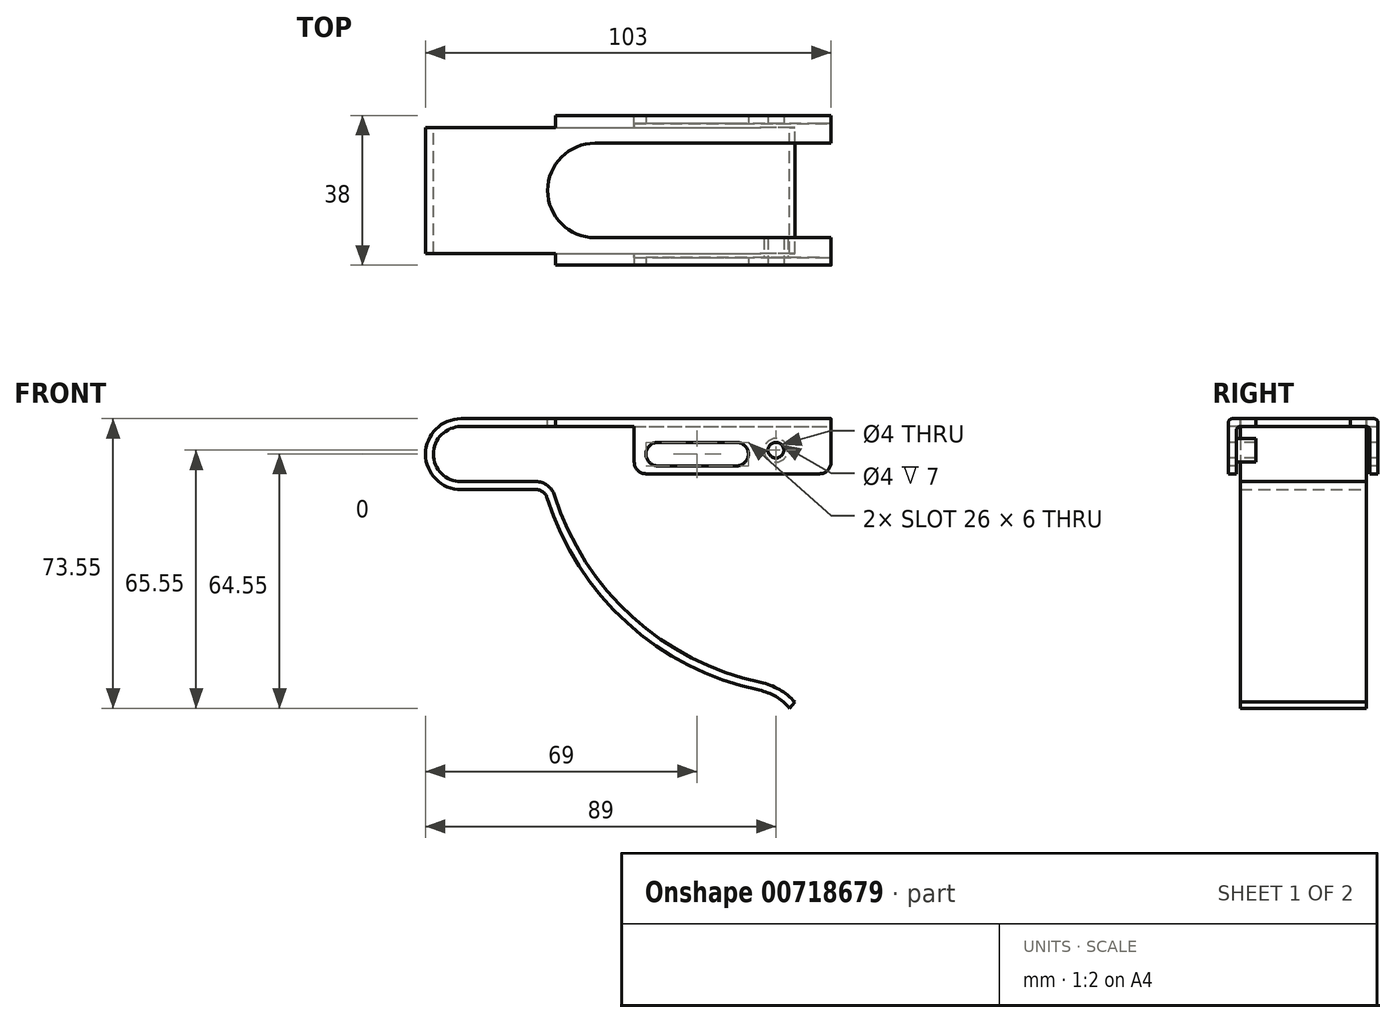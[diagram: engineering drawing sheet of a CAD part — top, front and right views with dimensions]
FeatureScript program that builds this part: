
annotation { "Feature Type Name" : "Feature", "Feature Type Description" : "" }
export const myFeature = defineFeature(function(context is Context, id is Id, definition is map)
    precondition{}
    {
        {
            var Q0;
            Q0=qCreatedBy(makeId("Front.planeOp"),FACE);
            var sketch = newSketch(context, id + "F0", { "sketchPlane" : qUnion([Q0])});
            skArc(sketch, "E0", {"start": v(0, 9) * mm, "mid": v(-9, 0) * mm, "end": v(0, -9) * mm});
            skLineSegment(sketch, "E1", {"start": v(0, -9) * mm, "end": v(19, -9) * mm});
            skLineSegment(sketch, "E2", {"start": v(0, 9) * mm, "end": v(94, 9) * mm});
            skArc(sketch, "E3", {"start": v(21.86, -11.1) * mm, "mid": v(42.18, -42.83) * mm, "end": v(75.74, -59.96) * mm});
            skArc(sketch, "E4", {"start": v(83.5, -64.55) * mm, "mid": v(80, -61.61) * mm, "end": v(75.74, -59.96) * mm});
            skPoint(sketch, "E5.visualSharp", {"position": v(21.24, -9) * mm});
            skArc(sketch, "E5.filletArc", {"start": v(21.86, -11.1) * mm, "mid": v(20.77, -9.58) * mm, "end": v(19, -9) * mm});
            skLineSegment(sketch, "E6.0", {"start": v(0, 7) * mm, "end": v(94, 7) * mm});
            skArc(sketch, "E6.1", {"start": v(0, 7) * mm, "mid": v(-7, 0) * mm, "end": v(0, -7) * mm});
            skArc(sketch, "E6.2", {"start": v(84.8, -63) * mm, "mid": v(80.87, -59.8) * mm, "end": v(76.15, -58) * mm});
            skArc(sketch, "E6.3", {"start": v(23.77, -10.5) * mm, "mid": v(43.52, -41.35) * mm, "end": v(76.15, -58) * mm});
            skArc(sketch, "E6.4", {"start": v(23.77, -10.5) * mm, "mid": v(21.96, -7.97) * mm, "end": v(19, -7) * mm});
            skLineSegment(sketch, "E6.5", {"start": v(0, -7) * mm, "end": v(19, -7) * mm});
            skLineSegment(sketch, "E7", {"start": v(83.5, -64.55) * mm, "end": v(84.8, -63) * mm});
            skLineSegment(sketch, "E8", {"start": v(94, 9) * mm, "end": v(94, 7) * mm});
            skSolve(sketch);
        }
        {
            var Q0;
            Q0 = qSketchRegion(id + "F0", true);
            extrude(context, id + "F1", {"entities" : qUnion([Q0]), "depth" : 16 * mm, "offsetDistance" : 25 * mm});
        }
        {
            var Q0;
            Q0=makeQuery(id+"F1.opExtrude","SWEPT_FACE",FACE,{"disambiguationData":[OSD([sQuery(id+"F0.wireOp",EDGE,"E2")])]});
            var sketch = newSketch(context, id + "F2", { "sketchPlane" : qUnion([Q0])});
            skLineSegment(sketch, "E9.bottom", {"start": v(94, -16) * mm, "end": v(24, -16) * mm});
            skLineSegment(sketch, "E9.top", {"start": v(94, -19) * mm, "end": v(24, -19) * mm});
            skLineSegment(sketch, "E9.left", {"start": v(94, -16) * mm, "end": v(94, -19) * mm});
            skLineSegment(sketch, "E9.right", {"start": v(24, -16) * mm, "end": v(24, -19) * mm});
            skSolve(sketch);
        }
        {
            var Q0;
            Q0 = qSketchRegion(id + "F2", true);
            extrude(context, id + "F3", {"entities" : qUnion([Q0]), "operationType" : NewBodyOperationType.ADD, "oppositeDirection" : true, "depth" : 2 * mm, "offsetDistance" : 25 * mm});
        }
        {
            var Q0;
            Q0=makeQuery(id+"F3.opExtrude","SWEPT_FACE",FACE,{"disambiguationData":[OSD([sQuery(id+"F2.wireOp",EDGE,"E9.top")])]});
            var sketch = newSketch(context, id + "F4", { "sketchPlane" : qUnion([Q0])});
            skLineSegment(sketch, "E10.bottom", {"start": v(94, 9) * mm, "end": v(44, 9) * mm});
            skLineSegment(sketch, "E10.top", {"start": v(94, -5) * mm, "end": v(44, -5) * mm});
            skLineSegment(sketch, "E10.left", {"start": v(94, 9) * mm, "end": v(94, -5) * mm});
            skLineSegment(sketch, "E10.right", {"start": v(44, 9) * mm, "end": v(44, -5) * mm});
            skSolve(sketch);
        }
        {
            var Q0;
            Q0 = qSketchRegion(id + "F4", true);
            extrude(context, id + "F5", {"entities" : qUnion([Q0]), "operationType" : NewBodyOperationType.ADD, "oppositeDirection" : true, "depth" : 2 * mm, "offsetDistance" : 25 * mm});
        }
        {
            var Q0;
            Q0=makeQuery(id+"F3.opExtrude","CAP_EDGE",EDGE,{"disambiguationData":[OSD([sQuery(id+"F2.wireOp",EDGE,"E9.top")])],"isStart":true});
            var Q1;
            Q1=makeQuery(id+"F5.boolean.opBoolean","INTERSECT",EDGE,{"derivedFrom":[makeQuery(id+"F3.boolean.opBoolean","MERGE",FACE,{"derivedFrom":[makeQuery(id+"F1.opExtrude","SWEPT_FACE",FACE,{"disambiguationData":[OSD([sQuery(id+"F0.wireOp",EDGE,"E6.0")])]}),makeQuery(id+"F3.opExtrude","CAP_FACE",FACE,{"disambiguationData":[OSD([sQuery(id+"F2.wireOp",EDGE,"E9.bottom"),sQuery(id+"F2.wireOp",EDGE,"E9.top"),sQuery(id+"F2.wireOp",EDGE,"E9.left"),sQuery(id+"F2.wireOp",EDGE,"E9.right")])],"isStart":false})]}),makeQuery(id+"F5.opExtrude","CAP_FACE",FACE,{"disambiguationData":[OSD([sQuery(id+"F4.wireOp",EDGE,"E10.bottom"),sQuery(id+"F4.wireOp",EDGE,"E10.top"),sQuery(id+"F4.wireOp",EDGE,"E10.left"),sQuery(id+"F4.wireOp",EDGE,"E10.right")])],"isStart":false})]});
            fillet(context, id + "F6", {"entities" : qUnion([Q0, Q1]), "radius" : 1 * mm, "allowEdgeOverflow" : false});
        }
        {
            var Q0;
            Q0=makeQuery(id+"F1.opExtrude","SWEPT_BODY",BODY,{"disambiguationData":[OSD([sQuery(id+"F0.wireOp",EDGE,"E0"),sQuery(id+"F0.wireOp",EDGE,"E1"),sQuery(id+"F0.wireOp",EDGE,"E2"),sQuery(id+"F0.wireOp",EDGE,"E3"),sQuery(id+"F0.wireOp",EDGE,"E4"),sQuery(id+"F0.wireOp",EDGE,"E5.filletArc"),sQuery(id+"F0.wireOp",EDGE,"E6.0"),sQuery(id+"F0.wireOp",EDGE,"E6.1"),sQuery(id+"F0.wireOp",EDGE,"E6.2"),sQuery(id+"F0.wireOp",EDGE,"E6.3"),sQuery(id+"F0.wireOp",EDGE,"E6.4"),sQuery(id+"F0.wireOp",EDGE,"E6.5"),sQuery(id+"F0.wireOp",EDGE,"E7"),sQuery(id+"F0.wireOp",EDGE,"E8")])]});
            var Q1;
            Q1=qCreatedBy(makeId("Front.planeOp"),FACE);
            mirror(context, id + "F7", {"operationType" : NewBodyOperationType.ADD, "entities" : qUnion([Q0]), "mirrorPlane" : qUnion([Q1])});
        }
        {
            var Q0;
            {var subQ0=makeQuery(id+"F3.boolean.opBoolean","MERGE",FACE,{"derivedFrom":[makeQuery(id+"F1.opExtrude","SWEPT_FACE",FACE,{"disambiguationData":[OSD([sQuery(id+"F0.wireOp",EDGE,"E2")])]}),makeQuery(id+"F3.opExtrude","CAP_FACE",FACE,{"disambiguationData":[OSD([sQuery(id+"F2.wireOp",EDGE,"E9.bottom"),sQuery(id+"F2.wireOp",EDGE,"E9.top"),sQuery(id+"F2.wireOp",EDGE,"E9.left"),sQuery(id+"F2.wireOp",EDGE,"E9.right")])],"isStart":true})]});Q0=makeQuery(id+"F7.boolean.opBoolean","MERGE",FACE,{"derivedFrom":[subQ0,makeQuery(id+"F7.opPattern","COPY",FACE,{"derivedFrom":subQ0,"instanceName":"1"})]});}
            var sketch = newSketch(context, id + "F8", { "sketchPlane" : qUnion([Q0])});
            skArc(sketch, "E11", {"start": v(34, 12) * mm, "mid": v(22, 0) * mm, "end": v(34, -12) * mm});
            skLineSegment(sketch, "E12", {"start": v(34, -12) * mm, "end": v(94, -12) * mm});
            skLineSegment(sketch, "E13", {"start": v(34, 12) * mm, "end": v(94, 12) * mm});
            skLineSegment(sketch, "E14", {"start": v(94, 12) * mm, "end": v(94, -12) * mm});
            skSolve(sketch);
        }
        {
            var Q0;
            Q0 = qSketchRegion(id + "F8", true);
            extrude(context, id + "F9", {"entities" : qUnion([Q0]), "operationType" : NewBodyOperationType.REMOVE, "oppositeDirection" : true, "depth" : 2 * mm, "offsetDistance" : 25 * mm});
        }
        {
            var Q0;
            Q0=makeQuery(id+"F5.boolean.opBoolean","MERGE",FACE,{"derivedFrom":[makeQuery(id+"F3.opExtrude","SWEPT_FACE",FACE,{"disambiguationData":[OSD([sQuery(id+"F2.wireOp",EDGE,"E9.top")])]}),makeQuery(id+"F5.opExtrude","CAP_FACE",FACE,{"disambiguationData":[OSD([sQuery(id+"F4.wireOp",EDGE,"E10.bottom"),sQuery(id+"F4.wireOp",EDGE,"E10.top"),sQuery(id+"F4.wireOp",EDGE,"E10.left"),sQuery(id+"F4.wireOp",EDGE,"E10.right")])],"isStart":true})]});
            var sketch = newSketch(context, id + "F10", { "sketchPlane" : qUnion([Q0])});
            skLineSegment(sketch, "E15", {"start": v(50, 0) * mm, "end": v(70, 0) * mm});
            skArc(sketch, "E16.0.startCap", {"start": v(50, -3) * mm, "mid": v(47, 0) * mm, "end": v(50, 3) * mm});
            skArc(sketch, "E16.0.endCap", {"start": v(70, 3) * mm, "mid": v(73, 0) * mm, "end": v(70, -3) * mm});
            skLineSegment(sketch, "E16.0.left", {"start": v(50, 3) * mm, "end": v(70, 3) * mm});
            skLineSegment(sketch, "E16.0.right", {"start": v(50, -3) * mm, "end": v(70, -3) * mm});
            skSolve(sketch);
        }
        {
            var Q0;
            Q0 = qSketchRegion(id + "F10", true);
            extrude(context, id + "F11", {"entities" : qUnion([Q0]), "operationType" : NewBodyOperationType.REMOVE, "endBound" : BoundingType.THROUGH_ALL, "oppositeDirection" : true, "depth" : 25 * mm, "offsetDistance" : 25 * mm});
        }
        {
            var Q0;
            Q0=makeQuery(id+"F5.boolean.opBoolean","MERGE",FACE,{"derivedFrom":[makeQuery(id+"F3.opExtrude","SWEPT_FACE",FACE,{"disambiguationData":[OSD([sQuery(id+"F2.wireOp",EDGE,"E9.top")])]}),makeQuery(id+"F5.opExtrude","CAP_FACE",FACE,{"disambiguationData":[OSD([sQuery(id+"F4.wireOp",EDGE,"E10.bottom"),sQuery(id+"F4.wireOp",EDGE,"E10.top"),sQuery(id+"F4.wireOp",EDGE,"E10.left"),sQuery(id+"F4.wireOp",EDGE,"E10.right")])],"isStart":true})]});
            var sketch = newSketch(context, id + "F12", { "sketchPlane" : qUnion([Q0])});
            skPoint(sketch, "E17", {"position": v(80, 1) * mm});
            skSolve(sketch);
        }
        {
            var Q0;
            Q0=sQuery(id+"F12.wireOp",VERTEX,"E17");
            var Q1;
            Q1=makeQuery(id+"F1.opExtrude","SWEPT_BODY",BODY,{"disambiguationData":[OSD([sQuery(id+"F0.wireOp",EDGE,"E0"),sQuery(id+"F0.wireOp",EDGE,"E1"),sQuery(id+"F0.wireOp",EDGE,"E2"),sQuery(id+"F0.wireOp",EDGE,"E3"),sQuery(id+"F0.wireOp",EDGE,"E4"),sQuery(id+"F0.wireOp",EDGE,"E5.filletArc"),sQuery(id+"F0.wireOp",EDGE,"E6.0"),sQuery(id+"F0.wireOp",EDGE,"E6.1"),sQuery(id+"F0.wireOp",EDGE,"E6.2"),sQuery(id+"F0.wireOp",EDGE,"E6.3"),sQuery(id+"F0.wireOp",EDGE,"E6.4"),sQuery(id+"F0.wireOp",EDGE,"E6.5"),sQuery(id+"F0.wireOp",EDGE,"E7"),sQuery(id+"F0.wireOp",EDGE,"E8")])]});
            hole(context, id + "F13", {"style" : HoleStyle.SIMPLE, "endStyle" : HoleEndStyle.THROUGH, "holeDiameter" : 4 * mm, "majorDiameter" : 5 * mm, "isTappedThrough" : true, "tappedDepth" : 12 * mm, "tapClearance" : 3, "locations" : qUnion([Q0]), "scope" : qUnion([Q1])});
        }
        {
            var Q0;
            Q0=makeQuery(id+"F5.opExtrude","CAP_FACE",FACE,{"disambiguationData":[OSD([sQuery(id+"F4.wireOp",EDGE,"E10.bottom"),sQuery(id+"F4.wireOp",EDGE,"E10.top"),sQuery(id+"F4.wireOp",EDGE,"E10.left"),sQuery(id+"F4.wireOp",EDGE,"E10.right")])],"isStart":false});
            var sketch = newSketch(context, id + "F14", { "sketchPlane" : qUnion([Q0])});
            skCircle(sketch, "E18.0", {"center": v(-80, 1) * mm, "radius": 2 * mm});
            skCircle(sketch, "E19.0", {"center": v(-80, 1) * mm, "radius": 3 * mm});
            skSolve(sketch);
        }
        {
            var Q0;
            Q0 = qSketchRegion(id + "F14", true);
            extrude(context, id + "F15", {"entities" : qUnion([Q0]), "operationType" : NewBodyOperationType.ADD, "depth" : 5 * mm, "offsetDistance" : 25 * mm});
        }
        {
            var Q0;
            Q0=makeQuery(id+"F5.opExtrude","SWEPT_EDGE",EDGE,{"disambiguationData":[OSD([sQuery(id+"F4.wireOp",EDGE,"E10.top"),sQuery(id+"F4.wireOp",EDGE,"E10.left")])]});
            var Q1;
            Q1=makeQuery(id+"F7.opPattern","COPY",EDGE,{"derivedFrom":makeQuery(id+"F5.opExtrude","SWEPT_EDGE",EDGE,{"disambiguationData":[OSD([sQuery(id+"F4.wireOp",EDGE,"E10.top"),sQuery(id+"F4.wireOp",EDGE,"E10.left")])]}),"instanceName":"1"});
            var Q2;
            Q2=makeQuery(id+"F7.opPattern","COPY",EDGE,{"derivedFrom":makeQuery(id+"F5.opExtrude","SWEPT_EDGE",EDGE,{"disambiguationData":[OSD([sQuery(id+"F4.wireOp",EDGE,"E10.top"),sQuery(id+"F4.wireOp",EDGE,"E10.right")])]}),"instanceName":"1"});
            var Q3;
            Q3=makeQuery(id+"F5.opExtrude","SWEPT_EDGE",EDGE,{"disambiguationData":[OSD([sQuery(id+"F4.wireOp",EDGE,"E10.top"),sQuery(id+"F4.wireOp",EDGE,"E10.right")])]});
            fillet(context, id + "F16", {"entities" : qUnion([Q0, Q1, Q2, Q3]), "radius" : 3 * mm, "tangentPropagation" : true, "allowEdgeOverflow" : false});
        }
    });
